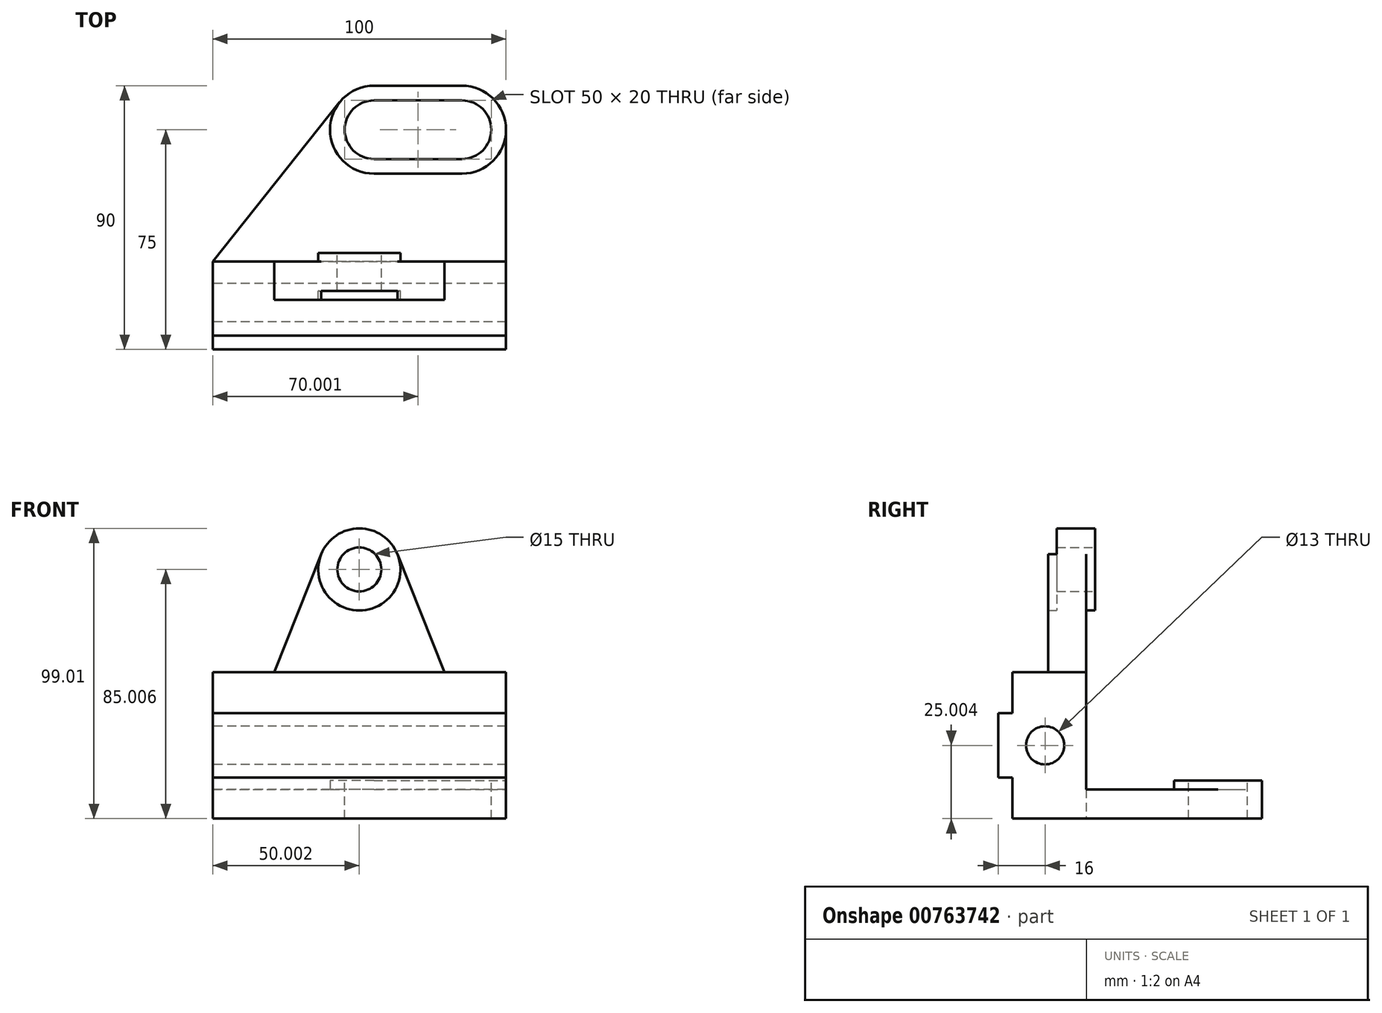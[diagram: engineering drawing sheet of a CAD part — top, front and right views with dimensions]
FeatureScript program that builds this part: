
annotation { "Feature Type Name" : "Feature", "Feature Type Description" : "" }
export const myFeature = defineFeature(function(context is Context, id is Id, definition is map)
    precondition{}
    {
        {
            var Q0;
            Q0=qCreatedBy(makeId("Front.planeOp"),FACE);
            var sketch = newSketch(context, id + "F0", { "sketchPlane" : qUnion([Q0])});
            skLineSegment(sketch, "E0.bottom", {"start": v(-71.7, -195.83) * mm, "end": v(28.3, -195.83) * mm});
            skLineSegment(sketch, "E0.top", {"start": v(-71.7, -245.83) * mm, "end": v(28.3, -245.83) * mm});
            skLineSegment(sketch, "E0.left", {"start": v(-71.7, -195.83) * mm, "end": v(-71.7, -245.83) * mm});
            skLineSegment(sketch, "E0.right", {"start": v(28.3, -195.83) * mm, "end": v(28.3, -245.83) * mm});
            skSolve(sketch);
        }
        {
            var Q0;
            Q0=makeQuery(id+"F0.imprint","IMPRINT",FACE,{"disambiguationData":[TD([[makeQuery(id+"F0.imprint","IMPRINT",EDGE,{"derivedFrom":sQuery(id+"F0.wireOp",EDGE,"E0.bottom")}),-1.0]])]});
            extrude(context, id + "F1", {"entities" : qUnion([Q0]), "oppositeDirection" : true, "depth" : 30 * mm, "offsetDistance" : 25 * mm});
        }
        {
            var Q0;
            Q0=makeQuery(id+"F1.opExtrude","SWEPT_FACE",FACE,{"disambiguationData":[OSD([sQuery(id+"F0.wireOp",EDGE,"E0.left")])]});
            var sketch = newSketch(context, id + "F2", { "sketchPlane" : qUnion([Q0])});
            skLineSegment(sketch, "E1", {"start": v(0, -245.83) * mm, "end": v(-4.8, -245.83) * mm});
            skLineSegment(sketch, "E2", {"start": v(-4.8, -245.83) * mm, "end": v(-4.8, -231.83) * mm});
            skLineSegment(sketch, "E3", {"start": v(-4.8, -231.83) * mm, "end": v(0, -231.83) * mm});
            skLineSegment(sketch, "E4", {"start": v(0, -195.83) * mm, "end": v(-4.8, -195.83) * mm});
            skLineSegment(sketch, "E5", {"start": v(-4.8, -195.83) * mm, "end": v(-4.8, -209.83) * mm});
            skLineSegment(sketch, "E6", {"start": v(-4.8, -209.83) * mm, "end": v(0, -209.83) * mm});
            skLineSegment(sketch, "E7", {"start": v(0, -209.83) * mm, "end": v(0, -231.83) * mm});
            skLineSegment(sketch, "E8", {"start": v(-4.8, -245.83) * mm, "end": v(-15, -245.83) * mm});
            skCircle(sketch, "E9", {"center": v(-16, -220.83) * mm, "radius": 6.5 * mm});
            skSolve(sketch);
        }
        {
            var Q0;
            Q0=sQuery(id+"F2.wireOp",VERTEX,"E9.center");
            var Q1;
            Q1=makeQuery(id+"F1.opExtrude","SWEPT_BODY",BODY,{"disambiguationData":[OSD([sQuery(id+"F0.wireOp",EDGE,"E0.bottom"),sQuery(id+"F0.wireOp",EDGE,"E0.top"),sQuery(id+"F0.wireOp",EDGE,"E0.left"),sQuery(id+"F0.wireOp",EDGE,"E0.right")])]});
            hole(context, id + "F3", {"style" : HoleStyle.SIMPLE, "endStyle" : HoleEndStyle.THROUGH, "holeDiameter" : 13 * mm, "majorDiameter" : 5 * mm, "isTappedThrough" : true, "tappedDepth" : 12 * mm, "tapClearance" : 3, "locations" : qUnion([Q0]), "scope" : qUnion([Q1])});
        }
        {
            var Q0;
            Q0=makeQuery(id+"F1.opExtrude","SWEPT_FACE",FACE,{"disambiguationData":[OSD([sQuery(id+"F0.wireOp",EDGE,"E0.left")])]});
            var sketch = newSketch(context, id + "F4", { "sketchPlane" : qUnion([Q0])});
            skLineSegment(sketch, "E10", {"start": v(0, -245.83) * mm, "end": v(-4.8, -245.83) * mm});
            skLineSegment(sketch, "E11", {"start": v(-4.8, -245.83) * mm, "end": v(-4.8, -231.83) * mm});
            skLineSegment(sketch, "E12", {"start": v(-4.8, -231.83) * mm, "end": v(0, -231.83) * mm});
            skLineSegment(sketch, "E13", {"start": v(0, -231.83) * mm, "end": v(0, -245.83) * mm});
            skSolve(sketch);
        }
        {
            var Q0;
            Q0=makeQuery(id+"F4.imprint","IMPRINT",FACE,{"disambiguationData":[TD([[makeQuery(id+"F4.imprint","IMPRINT",EDGE,{"derivedFrom":sQuery(id+"F4.wireOp",EDGE,"E10")}),1.0]])]});
            extrude(context, id + "F5", {"entities" : qUnion([Q0]), "operationType" : NewBodyOperationType.REMOVE, "oppositeDirection" : true, "depth" : 100 * mm, "offsetDistance" : 25 * mm});
        }
        {
            var Q0;
            Q0=makeQuery(id+"F1.opExtrude","SWEPT_FACE",FACE,{"disambiguationData":[OSD([sQuery(id+"F0.wireOp",EDGE,"E0.left")])]});
            var sketch = newSketch(context, id + "F6", { "sketchPlane" : qUnion([Q0])});
            skLineSegment(sketch, "E14", {"start": v(0, -195.83) * mm, "end": v(-4.8, -195.83) * mm});
            skLineSegment(sketch, "E15", {"start": v(-4.8, -195.83) * mm, "end": v(-4.8, -209.83) * mm});
            skLineSegment(sketch, "E16", {"start": v(-4.8, -209.83) * mm, "end": v(0, -209.83) * mm});
            skLineSegment(sketch, "E17", {"start": v(0, -209.83) * mm, "end": v(0, -195.83) * mm});
            skSolve(sketch);
        }
        {
            var Q0;
            Q0=makeQuery(id+"F6.imprint","IMPRINT",FACE,{"disambiguationData":[TD([[makeQuery(id+"F6.imprint","IMPRINT",EDGE,{"derivedFrom":sQuery(id+"F6.wireOp",EDGE,"E14")}),-1.0]])]});
            extrude(context, id + "F7", {"entities" : qUnion([Q0]), "operationType" : NewBodyOperationType.REMOVE, "oppositeDirection" : true, "depth" : 100 * mm, "offsetDistance" : 25 * mm});
        }
        {
            var Q0;
            Q0=makeQuery(id+"F1.opExtrude","SWEPT_FACE",FACE,{"disambiguationData":[OSD([sQuery(id+"F0.wireOp",EDGE,"E0.top")])]});
            cPlane(context, id + "F8", {"entities" : qUnion([Q0]), "cplaneType" : CPlaneType.OFFSET, "offset" : 0 * mm, "width" : 150 * mm, "height" : 150 * mm});
        }
        {
            var Q0;
            Q0=makeQuery(id+"F1.opExtrude","CAP_FACE",FACE,{"disambiguationData":[OSD([sQuery(id+"F0.wireOp",EDGE,"E0.bottom"),sQuery(id+"F0.wireOp",EDGE,"E0.top"),sQuery(id+"F0.wireOp",EDGE,"E0.left"),sQuery(id+"F0.wireOp",EDGE,"E0.right")])],"isStart":false});
            var sketch = newSketch(context, id + "F9", { "sketchPlane" : qUnion([Q0])});
            skLineSegment(sketch, "E18", {"start": v(-28.3, -245.83) * mm, "end": v(-28.3, -235.83) * mm});
            skLineSegment(sketch, "E19", {"start": v(71.7, -245.83) * mm, "end": v(71.7, -235.83) * mm});
            skLineSegment(sketch, "E20", {"start": v(71.7, -235.83) * mm, "end": v(-28.3, -235.83) * mm});
            skLineSegment(sketch, "E21", {"start": v(-28.3, -245.83) * mm, "end": v(71.7, -245.83) * mm});
            skLineSegment(sketch, "E22", {"start": v(21.7, -235.83) * mm, "end": v(21.7, -245.83) * mm});
            skSolve(sketch);
        }
        {
            var Q0;
            Q0=qCreatedBy(id+"F8.planeOp",FACE);
            var sketch = newSketch(context, id + "F10", { "sketchPlane" : qUnion([Q0])});
            skLineSegment(sketch, "E23", {"start": v(-70.1, -75) * mm, "end": v(66.85, -75) * mm, "construction": true});
            skLineSegment(sketch, "E24", {"start": v(13.3, -91.67) * mm, "end": v(13.3, -47.11) * mm, "construction": true});
            skLineSegment(sketch, "E25", {"start": v(-16.7, -91.11) * mm, "end": v(-16.7, -45.5) * mm, "construction": true});
            skArc(sketch, "E26", {"start": v(-28.43, -84.34) * mm, "mid": v(-23.21, -88.51) * mm, "end": v(-16.7, -90) * mm});
            skArc(sketch, "E27", {"start": v(13.3, -90) * mm, "mid": v(23.9, -85.6) * mm, "end": v(28.3, -75) * mm});
            skLineSegment(sketch, "E28", {"start": v(28.3, -30) * mm, "end": v(28.3, -75) * mm});
            skLineSegment(sketch, "E29", {"start": v(13.3, -90) * mm, "end": v(-16.7, -90) * mm});
            skLineSegment(sketch, "E30", {"start": v(28.3, -30) * mm, "end": v(-71.7, -30) * mm});
            skLineSegment(sketch, "E31", {"start": v(-71.7, -30) * mm, "end": v(-28.43, -84.34) * mm});
            skSolve(sketch);
        }
        {
            var Q0;
            Q0=makeQuery(id+"F10.imprint","IMPRINT",FACE,{"disambiguationData":[TD([[makeQuery(id+"F10.imprint","IMPRINT",EDGE,{"derivedFrom":sQuery(id+"F10.wireOp",EDGE,"E26")}),1.0]])]});
            extrude(context, id + "F11", {"entities" : qUnion([Q0]), "operationType" : NewBodyOperationType.ADD, "oppositeDirection" : true, "depth" : 10 * mm, "offsetDistance" : 25 * mm});
        }
        {
            var Q0;
            Q0=makeQuery(id+"F11.opExtrude","CAP_FACE",FACE,{"disambiguationData":[OSD([sQuery(id+"F10.wireOp",EDGE,"E26"),sQuery(id+"F10.wireOp",EDGE,"E27"),sQuery(id+"F10.wireOp",EDGE,"E28"),sQuery(id+"F10.wireOp",EDGE,"E29"),sQuery(id+"F10.wireOp",EDGE,"E30"),sQuery(id+"F10.wireOp",EDGE,"E31")])],"isStart":false});
            var sketch = newSketch(context, id + "F12", { "sketchPlane" : qUnion([Q0])});
            skArc(sketch, "E32", {"start": v(13.3, 60) * mm, "mid": v(28.3, 75) * mm, "end": v(13.3, 90) * mm});
            skArc(sketch, "E33", {"start": v(-16.7, 90) * mm, "mid": v(-31.7, 75) * mm, "end": v(-16.7, 60) * mm});
            skLineSegment(sketch, "E34", {"start": v(-16.7, 60) * mm, "end": v(13.3, 60) * mm});
            skLineSegment(sketch, "E35", {"start": v(13.3, 90) * mm, "end": v(-16.7, 90) * mm});
            skSolve(sketch);
        }
        {
            var Q0;
            {var subQ2=sQuery(id+"F12.wireOp",EDGE,"E34");Q0=makeQuery(id+"F12.imprint","IMPRINT",FACE,{"disambiguationData":[TD([[makeQuery(id+"F12.imprint","IMPRINT",EDGE,{"derivedFrom":subQ2}),1.0]])]});}
            extrude(context, id + "F13", {"entities" : qUnion([Q0]), "operationType" : NewBodyOperationType.ADD, "depth" : 3 * mm, "offsetDistance" : 25 * mm});
        }
        {
            var Q0;
            Q0=makeQuery(id+"F13.opExtrude","CAP_FACE",FACE,{"disambiguationData":[OSD([sQuery(id+"F12.wireOp",EDGE,"E32"),sQuery(id+"F12.wireOp",EDGE,"E33"),sQuery(id+"F12.wireOp",EDGE,"E34"),sQuery(id+"F12.wireOp",EDGE,"E35")])],"isStart":false});
            var sketch = newSketch(context, id + "F14", { "sketchPlane" : qUnion([Q0])});
            skArc(sketch, "E36", {"start": v(13.3, 65) * mm, "mid": v(23.3, 75) * mm, "end": v(13.3, 85) * mm});
            skArc(sketch, "E37", {"start": v(-16.7, 85) * mm, "mid": v(-26.7, 75) * mm, "end": v(-16.7, 65) * mm});
            skLineSegment(sketch, "E38", {"start": v(-16.7, 85) * mm, "end": v(13.3, 85) * mm});
            skLineSegment(sketch, "E39", {"start": v(13.3, 65) * mm, "end": v(-16.7, 65) * mm});
            skSolve(sketch);
        }
        {
            var Q0;
            Q0=makeQuery(id+"F14.imprint","IMPRINT",FACE,{"disambiguationData":[TD([[makeQuery(id+"F14.imprint","IMPRINT",EDGE,{"derivedFrom":sQuery(id+"F14.wireOp",EDGE,"E36")}),1.0]])]});
            extrude(context, id + "F15", {"entities" : qUnion([Q0]), "operationType" : NewBodyOperationType.REMOVE, "oppositeDirection" : true, "depth" : 13 * mm, "offsetDistance" : 25 * mm});
        }
        {
            var Q0;
            {var subQ1=makeQuery(id+"F1.opExtrude","CAP_EDGE",EDGE,{"disambiguationData":[OSD([sQuery(id+"F0.wireOp",EDGE,"E0.bottom")])],"isStart":false});Q0=makeQuery(id+"F9.imprint","IMPRINT",FACE,{"disambiguationData":[TD([[makeQuery(id+"F9.imprint","IMPRINT",EDGE,{"derivedFrom":subQ1}),1.0]])]});}
            var sketch = newSketch(context, id + "F16", { "sketchPlane" : qUnion([Q0])});
            skLineSegment(sketch, "E40", {"start": v(71.7, -195.82) * mm, "end": v(-28.3, -195.82) * mm});
            skLineSegment(sketch, "E41", {"start": v(71.7, -195.82) * mm, "end": v(50.7, -195.82) * mm});
            skLineSegment(sketch, "E42", {"start": v(-28.3, -195.82) * mm, "end": v(-7.3, -195.82) * mm});
            skCircle(sketch, "E43", {"center": v(21.7, -160.82) * mm, "radius": 14 * mm});
            skCircle(sketch, "E44", {"center": v(21.7, -160.82) * mm, "radius": 7.5 * mm});
            skLineSegment(sketch, "E45", {"start": v(-7.3, -195.82) * mm, "end": v(8.7, -155.65) * mm});
            skLineSegment(sketch, "E46", {"start": v(50.7, -195.82) * mm, "end": v(34.7, -155.65) * mm});
            skSolve(sketch);
        }
        {
            var Q0;
            Q0=makeQuery(id+"F16.imprint","IMPRINT",FACE,{"disambiguationData":[TD([[makeQuery(id+"F16.imprint","IMPRINT",EDGE,{"derivedFrom":sQuery(id+"F16.wireOp",EDGE,"E40")}),-1.0]])]});
            var Q1;
            Q1=makeQuery(id+"F16.imprint","IMPRINT",FACE,{"disambiguationData":[TD([[makeQuery(id+"F16.imprint","IMPRINT",EDGE,{"derivedFrom":sQuery(id+"F16.wireOp",EDGE,"E44")}),-1.0]])]});
            extrude(context, id + "F17", {"entities" : qUnion([Q0, Q1]), "oppositeDirection" : true, "depth" : 10 * mm, "offsetDistance" : 25 * mm});
        }
        {
            var Q0;
            Q0=makeQuery(id+"F17.opExtrude","CAP_FACE",FACE,{"disambiguationData":[OSD([sQuery(id+"F16.wireOp",EDGE,"E40"),sQuery(id+"F16.wireOp",EDGE,"E43"),sQuery(id+"F16.wireOp",EDGE,"E44"),sQuery(id+"F16.wireOp",EDGE,"E45"),sQuery(id+"F16.wireOp",EDGE,"E46")])],"isStart":true});
            var sketch = newSketch(context, id + "F18", { "sketchPlane" : qUnion([Q0])});
            skCircle(sketch, "E47", {"center": v(21.7, -160.82) * mm, "radius": 14 * mm});
            skSolve(sketch);
        }
        {
            var Q0;
            Q0=makeQuery(id+"F18.imprint","IMPRINT",FACE,{"disambiguationData":[TD([[makeQuery(id+"F18.imprint","IMPRINT",EDGE,{"derivedFrom":makeQuery(id+"F17.opExtrude","CAP_EDGE",EDGE,{"disambiguationData":[OSD([sQuery(id+"F16.wireOp",EDGE,"E44")])],"isStart":true})}),-1.0]])]});
            extrude(context, id + "F19", {"entities" : qUnion([Q0]), "operationType" : NewBodyOperationType.ADD, "endBound" : BoundingType.SYMMETRIC, "depth" : 6 * mm, "offsetDistance" : 25 * mm});
        }
        {
            var Q0;
            Q0=makeQuery(id+"F17.opExtrude","CAP_FACE",FACE,{"disambiguationData":[OSD([sQuery(id+"F16.wireOp",EDGE,"E40"),sQuery(id+"F16.wireOp",EDGE,"E43"),sQuery(id+"F16.wireOp",EDGE,"E44"),sQuery(id+"F16.wireOp",EDGE,"E45"),sQuery(id+"F16.wireOp",EDGE,"E46")])],"isStart":false});
            var sketch = newSketch(context, id + "F20", { "sketchPlane" : qUnion([Q0])});
            skCircle(sketch, "E48", {"center": v(-21.7, -160.82) * mm, "radius": 14 * mm});
            skSolve(sketch);
        }
        {
            var Q0;
            {var subQ0=sQuery(id+"F20.wireOp",EDGE,"E48");Q0=makeQuery(id+"F20.imprint","IMPRINT",FACE,{"disambiguationData":[TD([[makeQuery(id+"F20.imprint","IMPRINT",EDGE,{"disambiguationData":[OD(0.0)],"derivedFrom":subQ0}),-1.0]])]});}
            extrude(context, id + "F21", {"entities" : qUnion([Q0]), "operationType" : NewBodyOperationType.ADD, "endBound" : BoundingType.SYMMETRIC, "depth" : 6 * mm, "offsetDistance" : 25 * mm});
        }
    });
